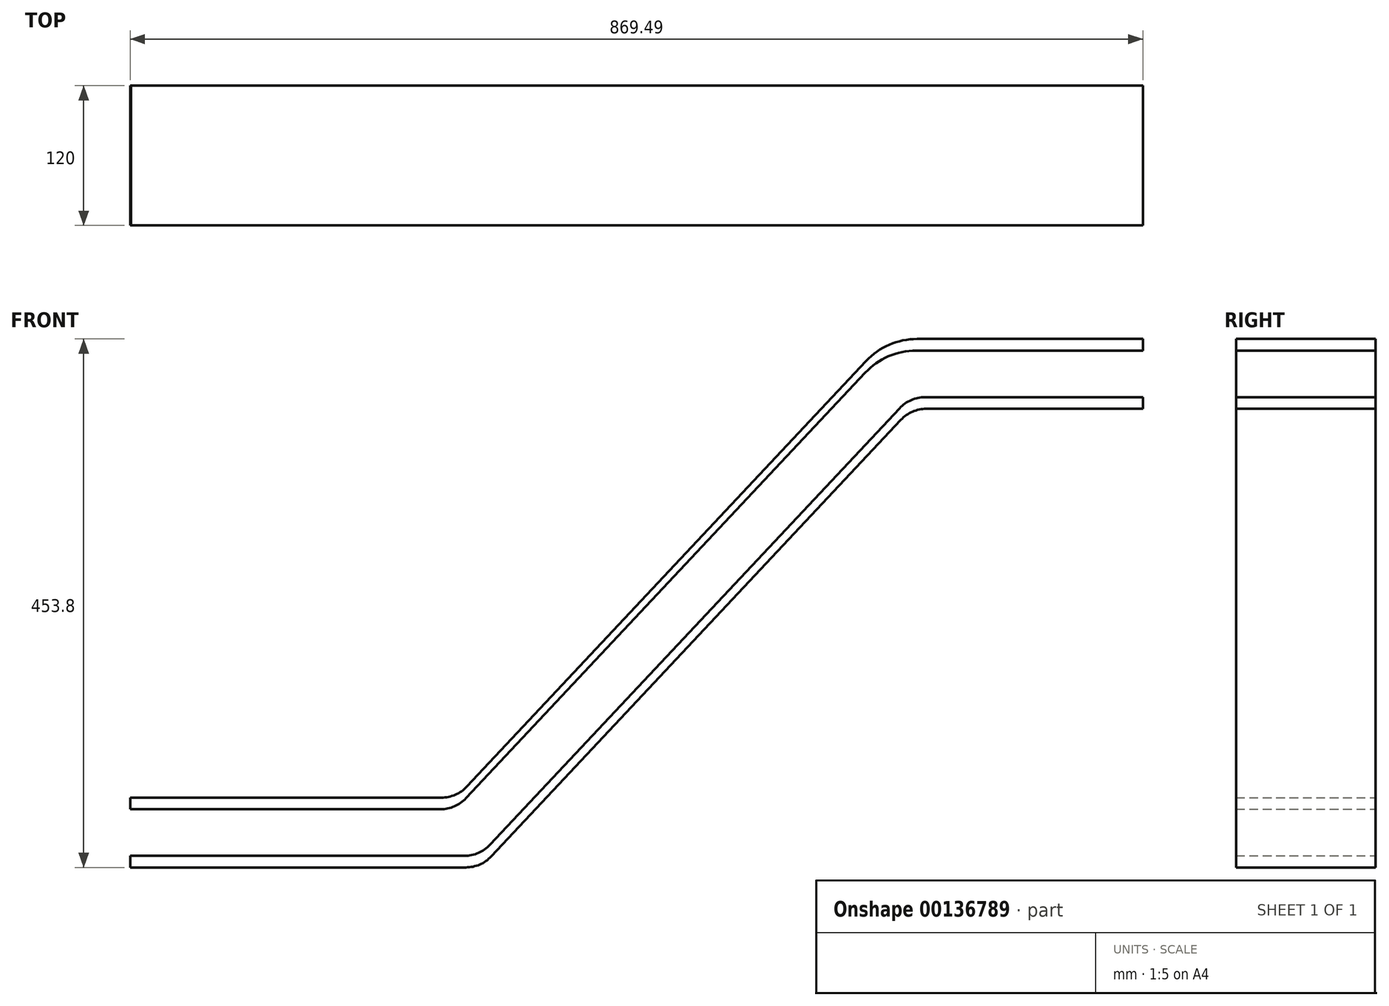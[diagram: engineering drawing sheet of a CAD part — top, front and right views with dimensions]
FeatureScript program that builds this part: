
annotation { "Feature Type Name" : "Feature", "Feature Type Description" : "" }
export const myFeature = defineFeature(function(context is Context, id is Id, definition is map)
    precondition{}
    {
        {
            var Q0;
            Q0=qCreatedBy(makeId("Front.planeOp"),FACE);
            var sketch = newSketch(context, id + "F0", { "sketchPlane" : qUnion([Q0])});
            skLineSegment(sketch, "E0", {"start": v(0, 0) * mm, "end": v(287.01, 0) * mm});
            skLineSegment(sketch, "E1", {"start": v(308.89, 9.47) * mm, "end": v(660.6, 384.33) * mm});
            skLineSegment(sketch, "E2", {"start": v(682.48, 393.8) * mm, "end": v(869.49, 393.8) * mm});
            skLineSegment(sketch, "E3", {"start": v(0, 40) * mm, "end": v(266.4, 40) * mm});
            skLineSegment(sketch, "E4", {"start": v(869.49, 433.8) * mm, "end": v(674.85, 433.8) * mm});
            skLineSegment(sketch, "E5", {"start": v(288.27, 49.47) * mm, "end": v(631.1, 414.85) * mm});
            skPoint(sketch, "E6.visualSharp", {"position": v(279.38, 40) * mm});
            skArc(sketch, "E6.filletArc", {"start": v(266.4, 40) * mm, "mid": v(278.32, 42.47) * mm, "end": v(288.27, 49.47) * mm});
            skPoint(sketch, "E7.visualSharp", {"position": v(300, 0) * mm});
            skArc(sketch, "E7.filletArc", {"start": v(287.01, 0) * mm, "mid": v(298.93, 2.47) * mm, "end": v(308.89, 9.47) * mm});
            skPoint(sketch, "E8.visualSharp", {"position": v(648.87, 433.8) * mm});
            skArc(sketch, "E8.filletArc", {"start": v(674.85, 433.8) * mm, "mid": v(651.01, 428.86) * mm, "end": v(631.1, 414.85) * mm});
            skPoint(sketch, "E9.visualSharp", {"position": v(669.49, 393.8) * mm});
            skArc(sketch, "E9.filletArc", {"start": v(682.48, 393.8) * mm, "mid": v(670.56, 391.33) * mm, "end": v(660.6, 384.33) * mm});
            skLineSegment(sketch, "E10", {"start": v(0, 40) * mm, "end": v(0, 50) * mm});
            skLineSegment(sketch, "E11", {"start": v(869.49, 433.8) * mm, "end": v(869.49, 443.8) * mm});
            skLineSegment(sketch, "E12", {"start": v(0.79, 49.96) * mm, "end": v(267.18, 49.96) * mm});
            skLineSegment(sketch, "E13", {"start": v(694.29, 443.76) * mm, "end": v(675.64, 443.76) * mm});
            skLineSegment(sketch, "E14", {"start": v(289.06, 59.44) * mm, "end": v(631.88, 424.82) * mm});
            skArc(sketch, "E15.filletArc", {"start": v(267.18, 49.96) * mm, "mid": v(279.1, 52.43) * mm, "end": v(289.06, 59.44) * mm});
            skArc(sketch, "E16.filletArc", {"start": v(675.64, 443.76) * mm, "mid": v(651.8, 438.82) * mm, "end": v(631.88, 424.82) * mm});
            skLineSegment(sketch, "E17", {"start": v(0, 50) * mm, "end": v(0.79, 49.96) * mm});
            skLineSegment(sketch, "E18", {"start": v(694.29, 443.76) * mm, "end": v(869.49, 443.8) * mm});
            skLineSegment(sketch, "E19", {"start": v(0, 0) * mm, "end": v(0, -10) * mm});
            skLineSegment(sketch, "E20", {"start": v(869.49, 393.8) * mm, "end": v(869.49, 383.8) * mm});
            skLineSegment(sketch, "E21", {"start": v(1.14, -9.99) * mm, "end": v(288.15, -9.99) * mm});
            skLineSegment(sketch, "E22", {"start": v(310.02, -0.51) * mm, "end": v(661.74, 374.34) * mm});
            skLineSegment(sketch, "E23", {"start": v(683.61, 383.81) * mm, "end": v(869.49, 383.81) * mm});
            skArc(sketch, "E24.filletArc", {"start": v(288.15, -9.99) * mm, "mid": v(300.07, -7.52) * mm, "end": v(310.02, -0.51) * mm});
            skArc(sketch, "E25.filletArc", {"start": v(683.61, 383.81) * mm, "mid": v(671.7, 381.34) * mm, "end": v(661.74, 374.34) * mm});
            skLineSegment(sketch, "E26", {"start": v(1.14, -9.99) * mm, "end": v(0, -10) * mm});
            skSolve(sketch);
        }
        {
            var Q0;
            Q0 = qSketchRegion(id + "F0", true);
            extrude(context, id + "F1", {"entities" : qUnion([Q0]), "depth" : 120 * mm});
        }
    });
